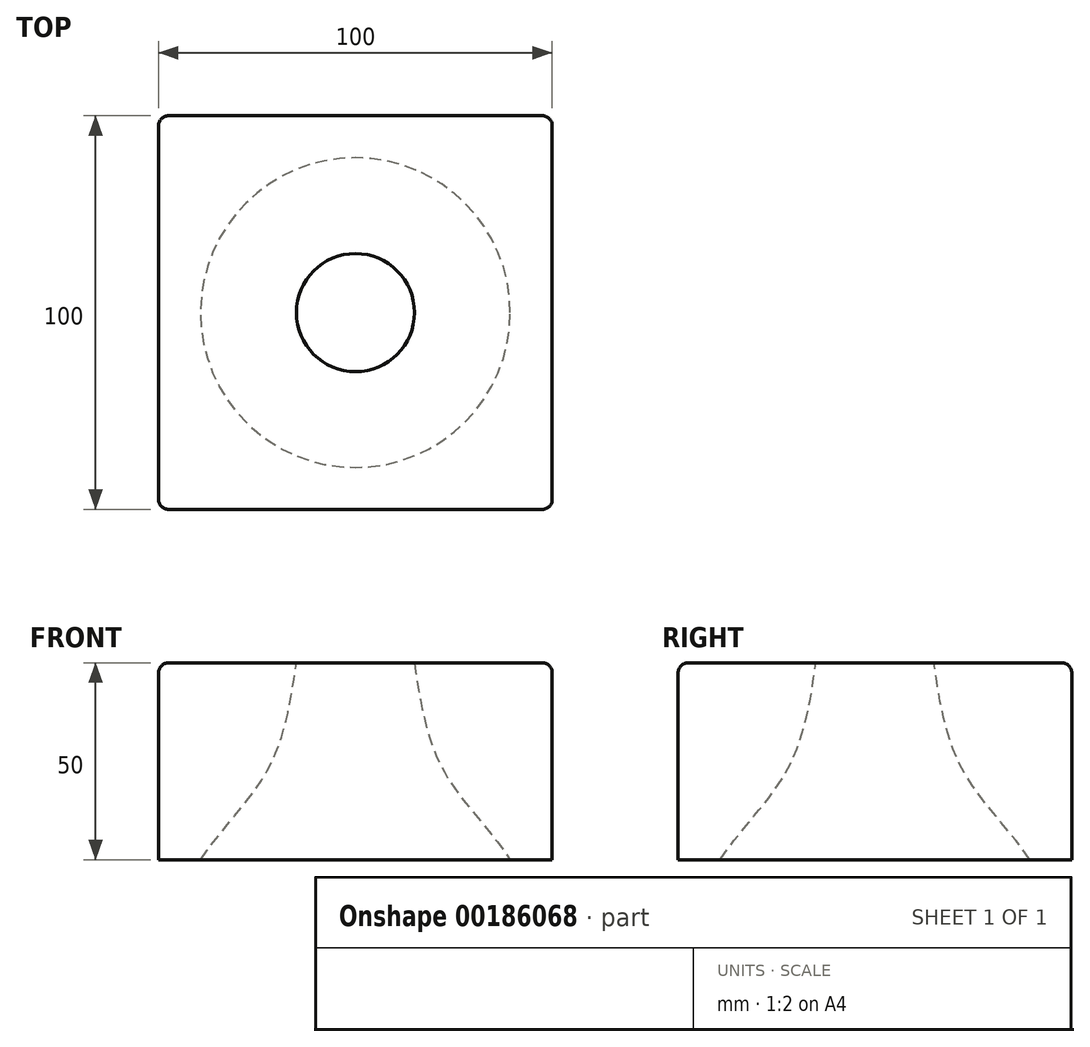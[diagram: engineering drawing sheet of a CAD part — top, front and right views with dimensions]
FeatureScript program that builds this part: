
annotation { "Feature Type Name" : "Feature", "Feature Type Description" : "" }
export const myFeature = defineFeature(function(context is Context, id is Id, definition is map)
    precondition{}
    {
        {
            var Q0;
            Q0=qCreatedBy(makeId("Top.planeOp"),FACE);
            var sketch = newSketch(context, id + "F0", { "sketchPlane" : qUnion([Q0])});
            skLineSegment(sketch, "E0.bottom", {"start": v(50, 50) * mm, "end": v(-50, 50) * mm});
            skLineSegment(sketch, "E0.top", {"start": v(50, -50) * mm, "end": v(-50, -50) * mm});
            skLineSegment(sketch, "E0.left", {"start": v(50, 50) * mm, "end": v(50, -50) * mm});
            skLineSegment(sketch, "E0.right", {"start": v(-50, 50) * mm, "end": v(-50, -50) * mm});
            skPoint(sketch, "E0.middle", {"position": v(0, 0) * mm});
            skSolve(sketch);
        }
        {
            var Q0;
            Q0=makeQuery(id+"F0.imprint","IMPRINT",FACE,{"disambiguationData":[TD([[makeQuery(id+"F0.imprint","IMPRINT",EDGE,{"derivedFrom":sQuery(id+"F0.wireOp",EDGE,"E0.bottom")}),1.0]])]});
            extrude(context, id + "F1", {"entities" : qUnion([Q0]), "depth" : 50 * mm});
        }
        {
            var Q0;
            Q0=qCreatedBy(makeId("Front.planeOp"),FACE);
            var sketch = newSketch(context, id + "F2", { "sketchPlane" : qUnion([Q0])});
            skLineSegment(sketch, "E1", {"start": v(-39.34, 0) * mm, "end": v(0, 0) * mm});
            skPoint(sketch, "E2", {"position": v(0, 0) * mm});
            skLineSegment(sketch, "E3", {"start": v(0, 0) * mm, "end": v(0, 50) * mm});
            skFitSpline(sketch, "E4", {"points": [v(-15, 50) * mm, v(-21.7, 23.9) * mm, v(-39.34, 0) * mm], "startDerivative": vector(-7.32, -51.57) * mm, "endDerivative": vector(-37.11, -54.23) * mm});
            skLineSegment(sketch, "E5", {"start": v(-15, 50) * mm, "end": v(0, 50) * mm});
            skPoint(sketch, "E6.endSnap0", {"position": v(-19.67, 0) * mm});
            skSolve(sketch);
        }
        {
            var Q0;
            Q0 = qSketchRegion(id + "F2", true);
            var Q1;
            Q1=sQuery(id+"F2.wireOp",EDGE,"E3");
            revolve(context, id + "F3", {"operationType" : NewBodyOperationType.REMOVE, "entities" : qUnion([Q0]), "axis" : qUnion([Q1]), "revolveType" : RevolveType.FULL, "oppositeDirection" : true});
        }
        {
            var Q0;
            Q0=makeQuery(id+"F1.opExtrude","CAP_EDGE",EDGE,{"disambiguationData":[OSD([sQuery(id+"F0.wireOp",EDGE,"E0.bottom")])],"isStart":false});
            var Q1;
            Q1=makeQuery(id+"F1.opExtrude","CAP_EDGE",EDGE,{"disambiguationData":[OSD([sQuery(id+"F0.wireOp",EDGE,"E0.left")])],"isStart":false});
            var Q2;
            Q2=makeQuery(id+"F1.opExtrude","CAP_EDGE",EDGE,{"disambiguationData":[OSD([sQuery(id+"F0.wireOp",EDGE,"E0.top")])],"isStart":false});
            var Q3;
            Q3=makeQuery(id+"F1.opExtrude","CAP_EDGE",EDGE,{"disambiguationData":[OSD([sQuery(id+"F0.wireOp",EDGE,"E0.right")])],"isStart":false});
            var Q4;
            Q4=makeQuery(id+"F1.opExtrude","SWEPT_EDGE",EDGE,{"disambiguationData":[OSD([sQuery(id+"F0.wireOp",EDGE,"E0.top"),sQuery(id+"F0.wireOp",EDGE,"E0.right")])]});
            var Q5;
            Q5=makeQuery(id+"F1.opExtrude","SWEPT_EDGE",EDGE,{"disambiguationData":[OSD([sQuery(id+"F0.wireOp",EDGE,"E0.top"),sQuery(id+"F0.wireOp",EDGE,"E0.left")])]});
            var Q6;
            Q6=makeQuery(id+"F1.opExtrude","SWEPT_EDGE",EDGE,{"disambiguationData":[OSD([sQuery(id+"F0.wireOp",EDGE,"E0.bottom"),sQuery(id+"F0.wireOp",EDGE,"E0.left")])]});
            var Q7;
            Q7=makeQuery(id+"F1.opExtrude","SWEPT_EDGE",EDGE,{"disambiguationData":[OSD([sQuery(id+"F0.wireOp",EDGE,"E0.bottom"),sQuery(id+"F0.wireOp",EDGE,"E0.right")])]});
            fillet(context, id + "F4", {"entities" : qUnion([Q0, Q1, Q2, Q3, Q4, Q5, Q6, Q7]), "radius" : 2.5 * mm, "tangentPropagation" : true, "allowEdgeOverflow" : false});
        }
    });
